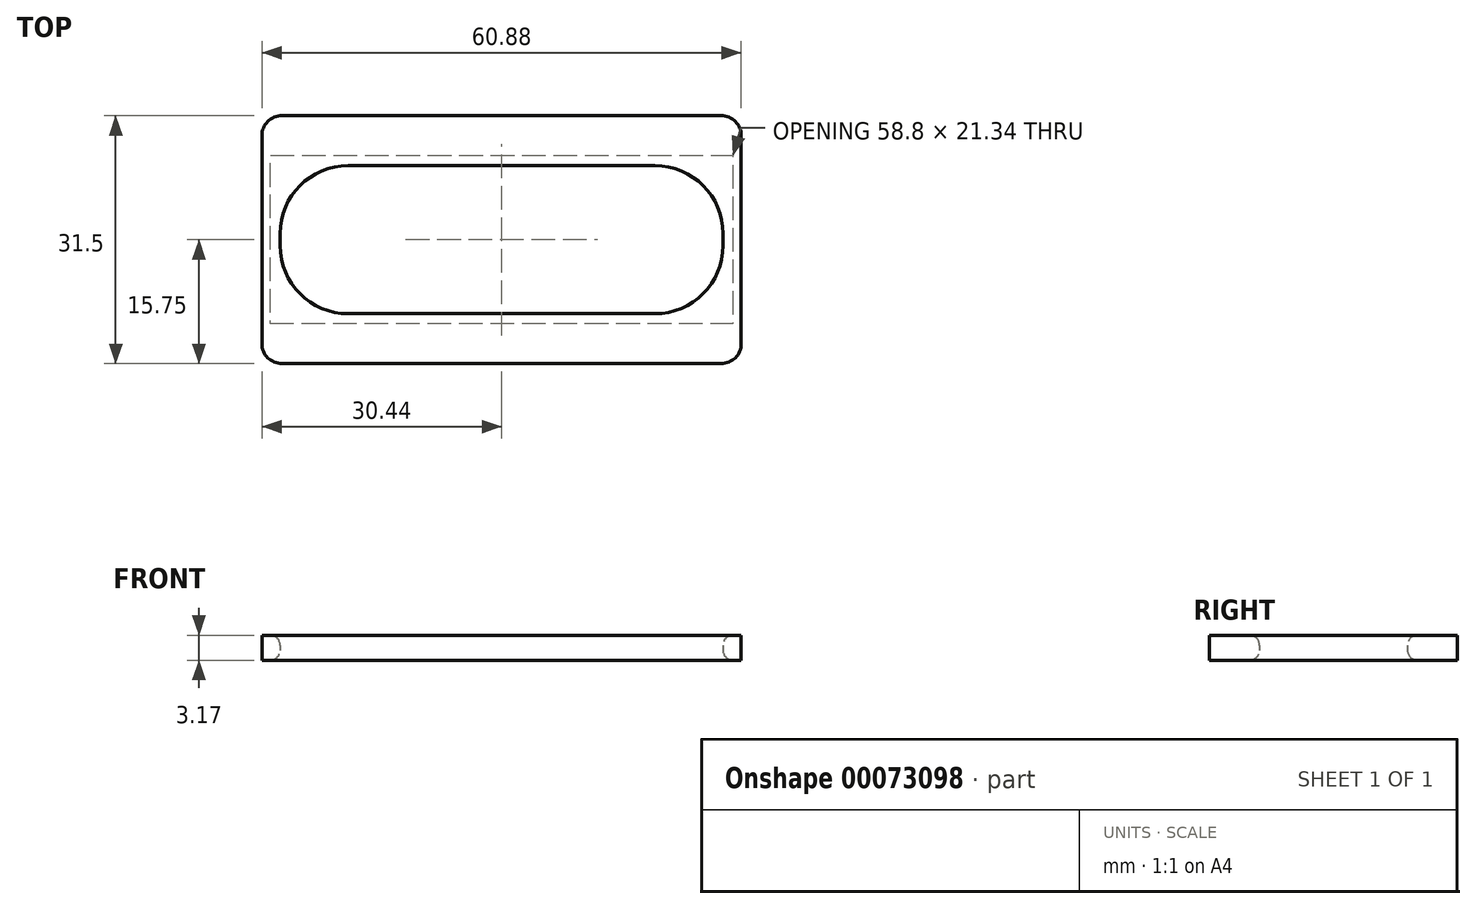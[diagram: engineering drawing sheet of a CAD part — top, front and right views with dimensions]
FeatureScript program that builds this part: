
annotation { "Feature Type Name" : "Feature", "Feature Type Description" : "" }
export const myFeature = defineFeature(function(context is Context, id is Id, definition is map)
    precondition{}
    {
        {
            var Q0;
            Q0=qCreatedBy(makeId("Top.planeOp"),FACE);
            var sketch = newSketch(context, id + "F0", { "sketchPlane" : qUnion([Q0])});
            skLineSegment(sketch, "E0.rect.bottom", {"start": v(27.9, 15.75) * mm, "end": v(-27.9, 15.75) * mm});
            skLineSegment(sketch, "E0.rect.top", {"start": v(27.9, -15.75) * mm, "end": v(-27.9, -15.75) * mm});
            skLineSegment(sketch, "E0.rect.left", {"start": v(30.44, 13.2) * mm, "end": v(30.44, -13.2) * mm});
            skLineSegment(sketch, "E0.rect.right", {"start": v(-30.44, 13.2) * mm, "end": v(-30.44, -13.2) * mm});
            skPoint(sketch, "E0.rect.middle", {"position": v(0, 0) * mm});
            skLineSegment(sketch, "E1.rect.bottom", {"start": v(19.5, -9.4) * mm, "end": v(-19.5, -9.4) * mm});
            skLineSegment(sketch, "E1.rect.top", {"start": v(19.5, 9.4) * mm, "end": v(-19.5, 9.4) * mm});
            skLineSegment(sketch, "E1.rect.left", {"start": v(28.13, -0.76) * mm, "end": v(28.13, 0.76) * mm});
            skLineSegment(sketch, "E1.rect.right", {"start": v(-28.13, -0.76) * mm, "end": v(-28.13, 0.76) * mm});
            skPoint(sketch, "E2.visualSharp", {"position": v(-28.13, 9.4) * mm});
            skArc(sketch, "E2.filletArc", {"start": v(-19.5, 9.4) * mm, "mid": v(-25.6, 6.87) * mm, "end": v(-28.13, 0.76) * mm});
            skPoint(sketch, "E3.visualSharp", {"position": v(-28.13, -9.4) * mm});
            skArc(sketch, "E3.filletArc", {"start": v(-28.13, -0.76) * mm, "mid": v(-25.6, -6.87) * mm, "end": v(-19.5, -9.4) * mm});
            skPoint(sketch, "E4.visualSharp", {"position": v(28.13, -9.4) * mm});
            skArc(sketch, "E4.filletArc", {"start": v(19.5, -9.4) * mm, "mid": v(25.6, -6.87) * mm, "end": v(28.13, -0.76) * mm});
            skPoint(sketch, "E5.visualSharp", {"position": v(28.13, 9.4) * mm});
            skArc(sketch, "E5.filletArc", {"start": v(28.13, 0.76) * mm, "mid": v(25.6, 6.87) * mm, "end": v(19.5, 9.4) * mm});
            skPoint(sketch, "E6.visualSharp", {"position": v(-30.44, 15.75) * mm});
            skArc(sketch, "E6.filletArc", {"start": v(-27.9, 15.75) * mm, "mid": v(-29.7, 15) * mm, "end": v(-30.44, 13.2) * mm});
            skPoint(sketch, "E7.visualSharp", {"position": v(30.44, 15.75) * mm});
            skArc(sketch, "E7.filletArc", {"start": v(30.44, 13.2) * mm, "mid": v(29.7, 15) * mm, "end": v(27.9, 15.75) * mm});
            skPoint(sketch, "E8.visualSharp", {"position": v(30.44, -15.75) * mm});
            skArc(sketch, "E8.filletArc", {"start": v(27.9, -15.75) * mm, "mid": v(29.7, -15) * mm, "end": v(30.44, -13.2) * mm});
            skPoint(sketch, "E9.visualSharp", {"position": v(-30.44, -15.75) * mm});
            skArc(sketch, "E9.filletArc", {"start": v(-30.44, -13.2) * mm, "mid": v(-29.7, -15) * mm, "end": v(-27.9, -15.75) * mm});
            skSolve(sketch);
        }
        {
            var Q0;
            Q0=makeQuery(id+"F0.imprint","IMPRINT",FACE,{"disambiguationData":[TD([[makeQuery(id+"F0.imprint","IMPRINT",EDGE,{"derivedFrom":sQuery(id+"F0.wireOp",EDGE,"E0.rect.bottom")}),1.0]])]});
            extrude(context, id + "F1", {"entities" : qUnion([Q0]), "depth" : 3.17 * mm});
        }
        {
            var Q0;
            Q0=makeQuery(id+"F1.opExtrude","CAP_EDGE",EDGE,{"disambiguationData":[OSD([sQuery(id+"F0.wireOp",EDGE,"E1.rect.bottom")])],"isStart":false});
            fillet(context, id + "F2", {"entities" : qUnion([Q0]), "radius" : 1.27 * mm, "tangentPropagation" : true, "allowEdgeOverflow" : false});
        }
        {
            var Q0;
            Q0=makeQuery(id+"F1.opExtrude","CAP_EDGE",EDGE,{"disambiguationData":[OSD([sQuery(id+"F0.wireOp",EDGE,"E1.rect.bottom")])],"isStart":true});
            var Q1;
            Q1=makeQuery(id+"F1.opExtrude","CAP_EDGE",EDGE,{"disambiguationData":[OSD([sQuery(id+"F0.wireOp",EDGE,"E4.filletArc")])],"isStart":true});
            var Q2;
            Q2=makeQuery(id+"F1.opExtrude","CAP_EDGE",EDGE,{"disambiguationData":[OSD([sQuery(id+"F0.wireOp",EDGE,"E3.filletArc")])],"isStart":true});
            var Q3;
            Q3=makeQuery(id+"F1.opExtrude","CAP_EDGE",EDGE,{"disambiguationData":[OSD([sQuery(id+"F0.wireOp",EDGE,"E2.filletArc")])],"isStart":true});
            var Q4;
            Q4=makeQuery(id+"F1.opExtrude","CAP_EDGE",EDGE,{"disambiguationData":[OSD([sQuery(id+"F0.wireOp",EDGE,"E1.rect.top")])],"isStart":true});
            var Q5;
            Q5=makeQuery(id+"F1.opExtrude","CAP_EDGE",EDGE,{"disambiguationData":[OSD([sQuery(id+"F0.wireOp",EDGE,"E5.filletArc")])],"isStart":true});
            var Q6;
            Q6=makeQuery(id+"F1.opExtrude","CAP_EDGE",EDGE,{"disambiguationData":[OSD([sQuery(id+"F0.wireOp",EDGE,"E1.rect.left")])],"isStart":true});
            var Q7;
            Q7=makeQuery(id+"F1.opExtrude","CAP_EDGE",EDGE,{"disambiguationData":[OSD([sQuery(id+"F0.wireOp",EDGE,"E1.rect.right")])],"isStart":true});
            fillet(context, id + "F3", {"entities" : qUnion([Q0, Q1, Q2, Q3, Q4, Q5, Q6, Q7]), "radius" : 1.27 * mm, "tangentPropagation" : true, "allowEdgeOverflow" : false});
        }
    });
